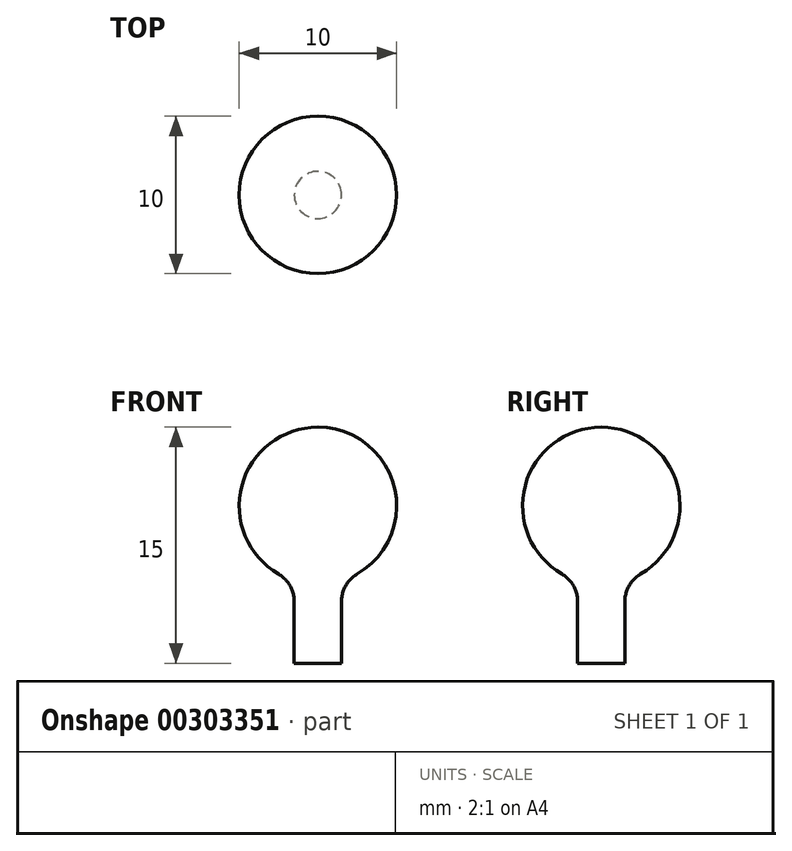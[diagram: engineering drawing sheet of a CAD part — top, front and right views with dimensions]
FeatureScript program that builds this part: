
annotation { "Feature Type Name" : "Feature", "Feature Type Description" : "" }
export const myFeature = defineFeature(function(context is Context, id is Id, definition is map)
    precondition{}
    {
        {
            var Q0;
            Q0=qCreatedBy(makeId("Front.planeOp"),FACE);
            var sketch = newSketch(context, id + "F0", { "sketchPlane" : qUnion([Q0])});
            skArc(sketch, "E0", {"start": v(1.5, -4.77) * mm, "mid": v(4.94, 0.76) * mm, "end": v(0, 5) * mm});
            skLineSegment(sketch, "E1.bottom", {"start": v(1.5, -10) * mm, "end": v(0, -10) * mm});
            skLineSegment(sketch, "E1.top", {"start": v(1.5, 10) * mm, "end": v(-1.5, 10) * mm});
            skLineSegment(sketch, "E1.left", {"start": v(1.5, -10) * mm, "end": v(1.5, -4.77) * mm});
            skLineSegment(sketch, "E2", {"start": v(0, 11.93) * mm, "end": v(0, -15.44) * mm, "construction": true});
            skPoint(sketch, "E2.endSnap0", {"position": v(0, -10) * mm});
            skPoint(sketch, "E3.orphan", {"position": v(-1.5, -10) * mm});
            skLineSegment(sketch, "E4", {"start": v(0, 5) * mm, "end": v(0, -10) * mm});
            skSolve(sketch);
        }
        {
            var Q0;
            Q0 = qSketchRegion(id + "F0", true);
            var Q1;
            Q1=sQuery(id+"F0.wireOp",EDGE,"E4");
            revolve(context, id + "F1", {"entities" : qUnion([Q0]), "axis" : qUnion([Q1]), "revolveType" : RevolveType.FULL});
        }
        {
            var Q0;
            Q0=makeQuery(id+"F1.opRevolve","SWEPT_FACE",FACE,{"disambiguationData":[OSD([sQuery(id+"F0.wireOp",EDGE,"E0")])]});
            fillet(context, id + "F2", {"entities" : qUnion([Q0]), "radius" : 2 * mm, "tangentPropagation" : true, "allowEdgeOverflow" : false});
        }
    });
